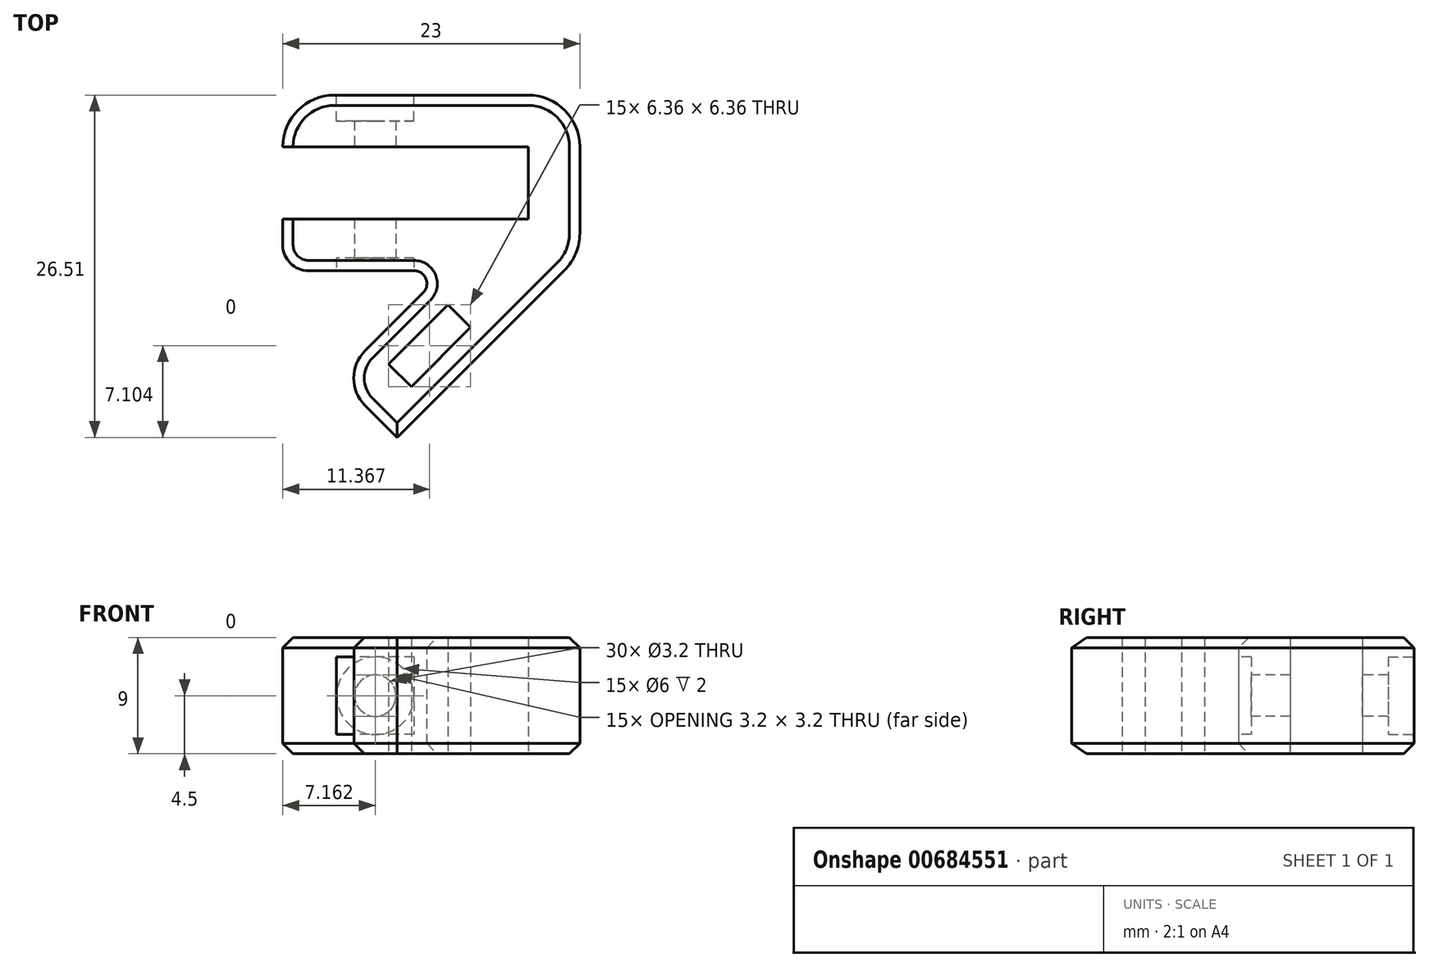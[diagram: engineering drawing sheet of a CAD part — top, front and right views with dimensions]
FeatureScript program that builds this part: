
annotation { "Feature Type Name" : "Feature", "Feature Type Description" : "" }
export const myFeature = defineFeature(function(context is Context, id is Id, definition is map)
    precondition{}
    {
        {
            var Q0;
            Q0=qCreatedBy(makeId("Top.planeOp"),FACE);
            var sketch = newSketch(context, id + "F0", { "sketchPlane" : qUnion([Q0])});
            skLineSegment(sketch, "E0", {"start": v(0, 0) * mm, "end": v(0, 4) * mm});
            skLineSegment(sketch, "E1", {"start": v(0, 4) * mm, "end": v(19, 4) * mm});
            skLineSegment(sketch, "E2", {"start": v(19, 4) * mm, "end": v(19, 9.6) * mm});
            skLineSegment(sketch, "E3", {"start": v(19, 9.6) * mm, "end": v(0, 9.6) * mm});
            skLineSegment(sketch, "E4", {"start": v(0, 9.6) * mm, "end": v(0, 13.6) * mm});
            skLineSegment(sketch, "E5", {"start": v(0, 13.6) * mm, "end": v(23, 13.6) * mm});
            skLineSegment(sketch, "E6", {"start": v(23, 13.6) * mm, "end": v(23, 1.23) * mm});
            skLineSegment(sketch, "E7", {"start": v(23, 1.23) * mm, "end": v(8.86, -12.91) * mm});
            skLineSegment(sketch, "E8", {"start": v(8.86, -12.91) * mm, "end": v(4.26, -8.31) * mm});
            skLineSegment(sketch, "E9", {"start": v(4.26, -8.31) * mm, "end": v(12.58, 0) * mm});
            skLineSegment(sketch, "E10", {"start": v(12.58, 0) * mm, "end": v(0, 0) * mm});
            skSolve(sketch);
        }
        {
            var Q0;
            Q0=makeQuery(id+"F0.imprint","IMPRINT",FACE,{"disambiguationData":[TD([[makeQuery(id+"F0.imprint","IMPRINT",EDGE,{"derivedFrom":sQuery(id+"F0.wireOp",EDGE,"E0")}),-1.0]])]});
            extrude(context, id + "F1", {"entities" : qUnion([Q0]), "depth" : 9 * mm});
        }
        {
            var Q0;
            Q0=makeQuery(id+"F1.opExtrude","SWEPT_EDGE",EDGE,{"disambiguationData":[OSD([sQuery(id+"F0.wireOp",EDGE,"E5"),sQuery(id+"F0.wireOp",EDGE,"E6")])]});
            var Q1;
            Q1=makeQuery(id+"F1.opExtrude","SWEPT_EDGE",EDGE,{"disambiguationData":[OSD([sQuery(id+"F0.wireOp",EDGE,"E4"),sQuery(id+"F0.wireOp",EDGE,"E5")])]});
            var Q2;
            Q2=makeQuery(id+"F1.opExtrude","SWEPT_EDGE",EDGE,{"disambiguationData":[OSD([sQuery(id+"F0.wireOp",EDGE,"E6"),sQuery(id+"F0.wireOp",EDGE,"E7")])]});
            fillet(context, id + "F2", {"entities" : qUnion([Q0, Q1, Q2]), "radius" : 4 * mm, "tangentPropagation" : true, "allowEdgeOverflow" : false});
        }
        {
            var Q0;
            Q0=makeQuery(id+"F1.opExtrude","SWEPT_EDGE",EDGE,{"disambiguationData":[OSD([sQuery(id+"F0.wireOp",EDGE,"E9"),sQuery(id+"F0.wireOp",EDGE,"E10")])]});
            fillet(context, id + "F3", {"entities" : qUnion([Q0]), "radius" : 1 * mm, "tangentPropagation" : true, "allowEdgeOverflow" : false});
        }
        {
            var Q0;
            Q0=makeQuery(id+"F1.opExtrude","SWEPT_EDGE",EDGE,{"disambiguationData":[OSD([sQuery(id+"F0.wireOp",EDGE,"E0"),sQuery(id+"F0.wireOp",EDGE,"E10")])]});
            fillet(context, id + "F4", {"entities" : qUnion([Q0]), "radius" : 2 * mm, "tangentPropagation" : true, "allowEdgeOverflow" : false});
        }
        {
            var Q0;
            Q0=makeQuery(id+"F1.opExtrude","SWEPT_FACE",FACE,{"disambiguationData":[OSD([sQuery(id+"F0.wireOp",EDGE,"E10")])]});
            var sketch = newSketch(context, id + "F5", { "sketchPlane" : qUnion([Q0])});
            skLineSegment(sketch, "E11.bottom", {"start": v(10.16, 7.5) * mm, "end": v(4.16, 7.5) * mm});
            skLineSegment(sketch, "E11.top", {"start": v(10.16, 1.5) * mm, "end": v(4.16, 1.5) * mm});
            skLineSegment(sketch, "E11.left", {"start": v(10.16, 7.5) * mm, "end": v(10.16, 1.5) * mm});
            skLineSegment(sketch, "E11.right", {"start": v(4.16, 7.5) * mm, "end": v(4.16, 1.5) * mm});
            skSolve(sketch);
        }
        {
            var Q0;
            Q0=makeQuery(id+"F5.imprint","IMPRINT",FACE,{"disambiguationData":[TD([[makeQuery(id+"F5.imprint","IMPRINT",EDGE,{"derivedFrom":sQuery(id+"F5.wireOp",EDGE,"E11.bottom")}),1.0]])]});
            extrude(context, id + "F6", {"entities" : qUnion([Q0]), "operationType" : NewBodyOperationType.REMOVE, "oppositeDirection" : true, "depth" : 1 * mm});
        }
        {
            var Q0;
            Q0=makeQuery(id+"F6.boolean.opBoolean","COPY",FACE,{"derivedFrom":makeQuery(id+"F6.opExtrude","CAP_FACE",FACE,{"disambiguationData":[OSD([sQuery(id+"F5.wireOp",EDGE,"E11.bottom"),sQuery(id+"F5.wireOp",EDGE,"E11.top"),sQuery(id+"F5.wireOp",EDGE,"E11.left"),sQuery(id+"F5.wireOp",EDGE,"E11.right")])],"isStart":false})});
            var sketch = newSketch(context, id + "F7", { "sketchPlane" : qUnion([Q0])});
            skCircle(sketch, "E12", {"center": v(7.16, 4.5) * mm, "radius": 1.6 * mm});
            skSolve(sketch);
        }
        {
            var Q0;
            Q0=makeQuery(id+"F7.imprint","IMPRINT",FACE,{"disambiguationData":[TD([[makeQuery(id+"F7.imprint","IMPRINT",EDGE,{"derivedFrom":sQuery(id+"F7.wireOp",EDGE,"E12")}),1.0]])]});
            extrude(context, id + "F8", {"entities" : qUnion([Q0]), "operationType" : NewBodyOperationType.REMOVE, "endBound" : BoundingType.THROUGH_ALL, "oppositeDirection" : true, "depth" : 25 * mm});
        }
        {
            var Q0;
            Q0=makeQuery(id+"F1.opExtrude","SWEPT_FACE",FACE,{"disambiguationData":[OSD([sQuery(id+"F0.wireOp",EDGE,"E5")])]});
            var sketch = newSketch(context, id + "F9", { "sketchPlane" : qUnion([Q0])});
            skCircle(sketch, "E13", {"center": v(-7.16, 4.5) * mm, "radius": 3 * mm});
            skSolve(sketch);
        }
        {
            var Q0;
            Q0=makeQuery(id+"F9.imprint","IMPRINT",FACE,{"disambiguationData":[TD([[makeQuery(id+"F9.imprint","IMPRINT",EDGE,{"derivedFrom":sQuery(id+"F9.wireOp",EDGE,"E13")}),1.0]])]});
            extrude(context, id + "F10", {"entities" : qUnion([Q0]), "operationType" : NewBodyOperationType.REMOVE, "oppositeDirection" : true, "depth" : 2 * mm});
        }
        {
            var Q0;
            Q0=makeQuery(id+"F1.opExtrude","CAP_FACE",FACE,{"disambiguationData":[OSD([sQuery(id+"F0.wireOp",EDGE,"E0"),sQuery(id+"F0.wireOp",EDGE,"E1"),sQuery(id+"F0.wireOp",EDGE,"E2"),sQuery(id+"F0.wireOp",EDGE,"E3"),sQuery(id+"F0.wireOp",EDGE,"E4"),sQuery(id+"F0.wireOp",EDGE,"E5"),sQuery(id+"F0.wireOp",EDGE,"E6"),sQuery(id+"F0.wireOp",EDGE,"E7"),sQuery(id+"F0.wireOp",EDGE,"E8"),sQuery(id+"F0.wireOp",EDGE,"E9"),sQuery(id+"F0.wireOp",EDGE,"E10")])],"isStart":true});
            var sketch = newSketch(context, id + "F11", { "sketchPlane" : qUnion([Q0])});
            skLineSegment(sketch, "E14", {"start": v(14.55, 4.4) * mm, "end": v(9.95, 8.99) * mm});
            skLineSegment(sketch, "E15", {"start": v(9.95, 8.99) * mm, "end": v(8.18, 7.22) * mm});
            skLineSegment(sketch, "E16", {"start": v(8.18, 7.22) * mm, "end": v(12.78, 2.62) * mm});
            skLineSegment(sketch, "E17", {"start": v(12.78, 2.62) * mm, "end": v(14.55, 4.4) * mm});
            skSolve(sketch);
        }
        {
            var Q0;
            Q0=makeQuery(id+"F11.imprint","IMPRINT",FACE,{"disambiguationData":[TD([[makeQuery(id+"F11.imprint","IMPRINT",EDGE,{"derivedFrom":sQuery(id+"F11.wireOp",EDGE,"E14")}),1.0]])]});
            extrude(context, id + "F12", {"entities" : qUnion([Q0]), "operationType" : NewBodyOperationType.REMOVE, "endBound" : BoundingType.THROUGH_ALL, "oppositeDirection" : true, "depth" : 25 * mm});
        }
        {
            var Q0;
            Q0=makeQuery(id+"F1.opExtrude","SWEPT_EDGE",EDGE,{"disambiguationData":[OSD([sQuery(id+"F0.wireOp",EDGE,"E8"),sQuery(id+"F0.wireOp",EDGE,"E9")])]});
            fillet(context, id + "F13", {"entities" : qUnion([Q0]), "radius" : 3 * mm, "tangentPropagation" : true, "allowEdgeOverflow" : false});
        }
        {
            var Q0;
            Q0=makeQuery(id+"F1.opExtrude","CAP_EDGE",EDGE,{"disambiguationData":[OSD([sQuery(id+"F0.wireOp",EDGE,"E7")])],"isStart":false});
            var Q1;
            Q1=makeQuery(id+"F1.opExtrude","CAP_EDGE",EDGE,{"disambiguationData":[OSD([sQuery(id+"F0.wireOp",EDGE,"E10")])],"isStart":false});
            var Q2;
            Q2=makeQuery(id+"F1.opExtrude","CAP_EDGE",EDGE,{"disambiguationData":[OSD([sQuery(id+"F0.wireOp",EDGE,"E5")])],"isStart":true});
            var Q3;
            Q3=makeQuery(id+"F1.opExtrude","CAP_EDGE",EDGE,{"disambiguationData":[OSD([sQuery(id+"F0.wireOp",EDGE,"E10")])],"isStart":true});
            chamfer(context, id + "F14", {"entities" : qUnion([Q0, Q1, Q2, Q3]), "width" : 0.8 * mm, "tangentPropagation" : true});
        }
    });
